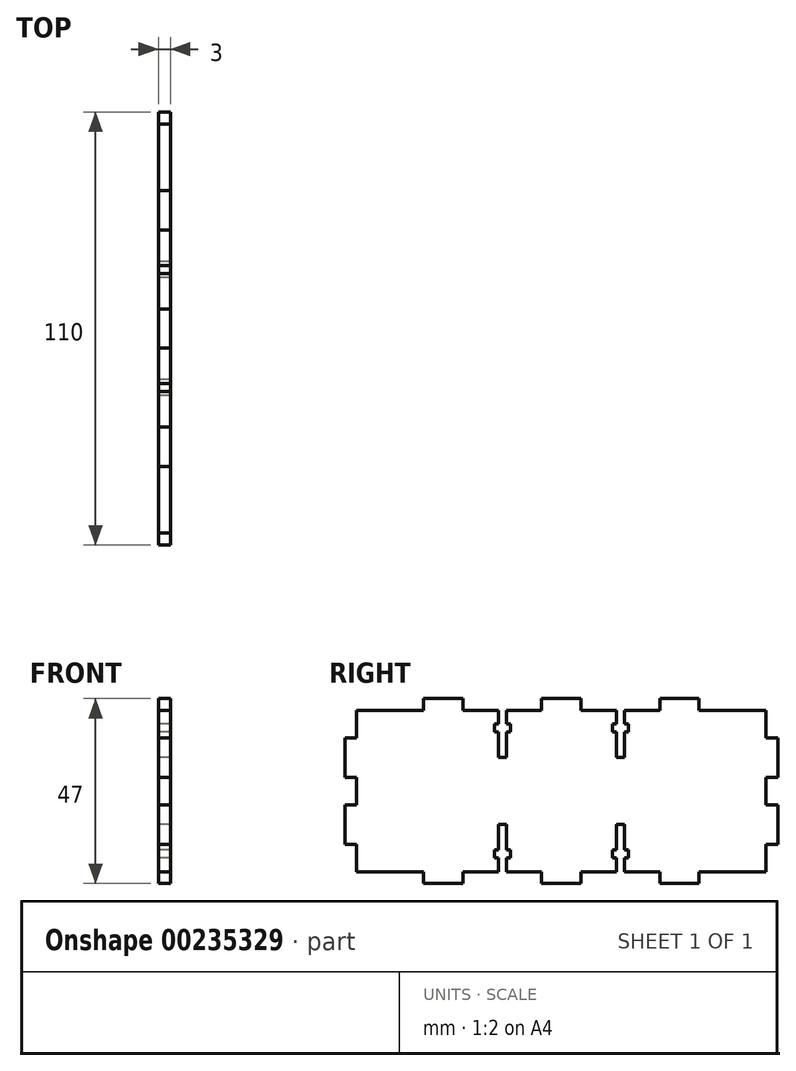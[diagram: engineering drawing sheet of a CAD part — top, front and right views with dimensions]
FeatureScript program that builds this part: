
annotation { "Feature Type Name" : "Feature", "Feature Type Description" : "" }
export const myFeature = defineFeature(function(context is Context, id is Id, definition is map)
    precondition{}
    {
        {
            var Q0;
            Q0=qCreatedBy(makeId("Right.planeOp"),FACE);
            var sketch = newSketch(context, id + "F0", { "sketchPlane" : qUnion([Q0])});
            skLineSegment(sketch, "E0", {"start": v(0, 0) * mm, "end": v(0, 7) * mm});
            skLineSegment(sketch, "E1", {"start": v(0, 7) * mm, "end": v(-3, 7) * mm});
            skLineSegment(sketch, "E2", {"start": v(-3, 7) * mm, "end": v(-3, 17) * mm});
            skLineSegment(sketch, "E3", {"start": v(-3, 17) * mm, "end": v(0, 17) * mm});
            skLineSegment(sketch, "E4", {"start": v(0, 17) * mm, "end": v(0, 24) * mm});
            skLineSegment(sketch, "E5", {"start": v(0, 24) * mm, "end": v(-3, 24) * mm});
            skLineSegment(sketch, "E6", {"start": v(-3, 24) * mm, "end": v(-3, 34) * mm});
            skLineSegment(sketch, "E7", {"start": v(-3, 34) * mm, "end": v(0, 34) * mm});
            skLineSegment(sketch, "E8", {"start": v(0, 34) * mm, "end": v(0, 41) * mm});
            skLineSegment(sketch, "E9", {"start": v(0, 41) * mm, "end": v(17, 41) * mm});
            skLineSegment(sketch, "E10", {"start": v(17, 41) * mm, "end": v(17, 44) * mm});
            skLineSegment(sketch, "E11", {"start": v(17, 44) * mm, "end": v(27, 44) * mm});
            skLineSegment(sketch, "E12", {"start": v(27, 44) * mm, "end": v(27, 41) * mm});
            skLineSegment(sketch, "E13", {"start": v(27, 41) * mm, "end": v(36, 41) * mm});
            skLineSegment(sketch, "E14", {"start": v(47, 41) * mm, "end": v(47, 44) * mm});
            skLineSegment(sketch, "E15", {"start": v(47, 44) * mm, "end": v(52, 44) * mm});
            skLineSegment(sketch, "E16.MirrorCS", {"start": v(47, 0) * mm, "end": v(47, -3) * mm});
            skLineSegment(sketch, "E17.MirrorCS", {"start": v(27, -3) * mm, "end": v(27, 0) * mm});
            skLineSegment(sketch, "E18.MirrorCS", {"start": v(17, 0) * mm, "end": v(17, -3) * mm});
            skLineSegment(sketch, "E19.MirrorCS", {"start": v(47, -3) * mm, "end": v(52, -3) * mm});
            skLineSegment(sketch, "E20.MirrorCS", {"start": v(27, 0) * mm, "end": v(33.54, 0) * mm});
            skLineSegment(sketch, "E21.MirrorCS", {"start": v(0, 0) * mm, "end": v(17, 0) * mm});
            skLineSegment(sketch, "E22.MirrorCS", {"start": v(17, -3) * mm, "end": v(27, -3) * mm});
            skLineSegment(sketch, "E23.MirrorCS", {"start": v(57, -3) * mm, "end": v(52, -3) * mm});
            skLineSegment(sketch, "E24.MirrorCS", {"start": v(57, 44) * mm, "end": v(52, 44) * mm});
            skLineSegment(sketch, "E25.top", {"start": v(36, 29) * mm, "end": v(38, 29) * mm});
            skLineSegment(sketch, "E25.left", {"start": v(36, 41) * mm, "end": v(36, 37.5) * mm});
            skLineSegment(sketch, "E25.right", {"start": v(38, 41) * mm, "end": v(38, 37.5) * mm});
            skLineSegment(sketch, "E26.MirrorCS", {"start": v(33.54, 41) * mm, "end": v(36, 41) * mm});
            skPoint(sketch, "E27.endSnap0", {"position": v(37, 29) * mm});
            skLineSegment(sketch, "E28.bottom", {"start": v(35, 37.5) * mm, "end": v(36, 37.5) * mm});
            skLineSegment(sketch, "E28.top", {"start": v(35, 35.5) * mm, "end": v(36, 35.5) * mm});
            skLineSegment(sketch, "E28.left", {"start": v(35, 37.5) * mm, "end": v(35, 35.5) * mm});
            skLineSegment(sketch, "E28.right", {"start": v(39, 37.5) * mm, "end": v(39, 35.5) * mm});
            skLineSegment(sketch, "E29.trimOffspring", {"start": v(38, 41) * mm, "end": v(47, 41) * mm});
            skLineSegment(sketch, "E30.trimOffspring", {"start": v(38, 41) * mm, "end": v(38.1, 41) * mm});
            skLineSegment(sketch, "E31.trimOffspring", {"start": v(38, 37.5) * mm, "end": v(39, 37.5) * mm});
            skLineSegment(sketch, "E32.trimOffspring", {"start": v(36, 35.5) * mm, "end": v(36, 29) * mm});
            skLineSegment(sketch, "E33.trimOffspring", {"start": v(38, 35.5) * mm, "end": v(38, 29) * mm});
            skLineSegment(sketch, "E34.trimOffspring", {"start": v(38, 35.5) * mm, "end": v(39, 35.5) * mm});
            skLineSegment(sketch, "E35.MirrorCS", {"start": v(38, 0) * mm, "end": v(38.1, 0) * mm});
            skLineSegment(sketch, "E36.MirrorCS", {"start": v(35, 3.5) * mm, "end": v(36, 3.5) * mm});
            skLineSegment(sketch, "E37.MirrorCS", {"start": v(38, 5.5) * mm, "end": v(39, 5.5) * mm});
            skLineSegment(sketch, "E38.MirrorCS", {"start": v(35, 5.5) * mm, "end": v(36, 5.5) * mm});
            skLineSegment(sketch, "E39.MirrorCS", {"start": v(38, 3.5) * mm, "end": v(39, 3.5) * mm});
            skLineSegment(sketch, "E40.MirrorCS", {"start": v(36, 12) * mm, "end": v(38, 12) * mm});
            skLineSegment(sketch, "E41.MirrorCS", {"start": v(36, 5.5) * mm, "end": v(36, 12) * mm});
            skLineSegment(sketch, "E42.MirrorCS", {"start": v(38, 5.5) * mm, "end": v(38, 12) * mm});
            skLineSegment(sketch, "E43.MirrorCS", {"start": v(35, 3.5) * mm, "end": v(35, 5.5) * mm});
            skLineSegment(sketch, "E44.MirrorCS", {"start": v(36, 0) * mm, "end": v(36, 3.5) * mm});
            skLineSegment(sketch, "E45.MirrorCS", {"start": v(39, 3.5) * mm, "end": v(39, 5.5) * mm});
            skLineSegment(sketch, "E46.MirrorCS", {"start": v(38, 0) * mm, "end": v(38, 3.5) * mm});
            skPoint(sketch, "E47.MirrorP", {"position": v(37, 12) * mm});
            skLineSegment(sketch, "E48.MirrorCS", {"start": v(33.54, 0) * mm, "end": v(36, 0) * mm});
            skLineSegment(sketch, "E49.trimOffspring", {"start": v(38, 0) * mm, "end": v(47, 0) * mm});
            skLineSegment(sketch, "E50", {"start": v(52, 44) * mm, "end": v(52, -3) * mm, "construction": true});
            skLineSegment(sketch, "E51.MirrorCS", {"start": v(66, 41) * mm, "end": v(65.9, 41) * mm});
            skLineSegment(sketch, "E52.MirrorCS", {"start": v(66, 0) * mm, "end": v(65.9, 0) * mm});
            skLineSegment(sketch, "E53.MirrorCS", {"start": v(69, 3.5) * mm, "end": v(68, 3.5) * mm});
            skLineSegment(sketch, "E54.MirrorCS", {"start": v(66, 5.5) * mm, "end": v(65, 5.5) * mm});
            skLineSegment(sketch, "E55.MirrorCS", {"start": v(66, 3.5) * mm, "end": v(65, 3.5) * mm});
            skLineSegment(sketch, "E56.MirrorCS", {"start": v(69, 5.5) * mm, "end": v(68, 5.5) * mm});
            skLineSegment(sketch, "E57.MirrorCS", {"start": v(69, 35.5) * mm, "end": v(68, 35.5) * mm});
            skLineSegment(sketch, "E58.MirrorCS", {"start": v(66, 37.5) * mm, "end": v(65, 37.5) * mm});
            skLineSegment(sketch, "E59.MirrorCS", {"start": v(66, 35.5) * mm, "end": v(65, 35.5) * mm});
            skLineSegment(sketch, "E60.MirrorCS", {"start": v(69, 37.5) * mm, "end": v(68, 37.5) * mm});
            skLineSegment(sketch, "E61.MirrorCS", {"start": v(68, 29) * mm, "end": v(66, 29) * mm});
            skLineSegment(sketch, "E62.MirrorCS", {"start": v(107, 17) * mm, "end": v(104, 17) * mm});
            skLineSegment(sketch, "E63.MirrorCS", {"start": v(68, 12) * mm, "end": v(66, 12) * mm});
            skLineSegment(sketch, "E64.MirrorCS", {"start": v(70.46, 41) * mm, "end": v(68, 41) * mm});
            skLineSegment(sketch, "E65.MirrorCS", {"start": v(65, 3.5) * mm, "end": v(65, 5.5) * mm});
            skLineSegment(sketch, "E66.MirrorCS", {"start": v(66, 41) * mm, "end": v(57, 41) * mm});
            skLineSegment(sketch, "E67.MirrorCS", {"start": v(77, 0) * mm, "end": v(70.46, 0) * mm});
            skLineSegment(sketch, "E68.MirrorCS", {"start": v(107, 7) * mm, "end": v(107, 17) * mm});
            skLineSegment(sketch, "E69.MirrorCS", {"start": v(104, 17) * mm, "end": v(104, 24) * mm});
            skLineSegment(sketch, "E70.MirrorCS", {"start": v(104, 24) * mm, "end": v(107, 24) * mm});
            skLineSegment(sketch, "E71.MirrorCS", {"start": v(66, 0) * mm, "end": v(66, 3.5) * mm});
            skLineSegment(sketch, "E72.MirrorCS", {"start": v(66, 41) * mm, "end": v(66, 37.5) * mm});
            skLineSegment(sketch, "E73.MirrorCS", {"start": v(107, 24) * mm, "end": v(107, 34) * mm});
            skLineSegment(sketch, "E74.MirrorCS", {"start": v(104, 34) * mm, "end": v(104, 41) * mm});
            skLineSegment(sketch, "E75.MirrorCS", {"start": v(107, 34) * mm, "end": v(104, 34) * mm});
            skLineSegment(sketch, "E76.MirrorCS", {"start": v(87, 41) * mm, "end": v(87, 44) * mm});
            skLineSegment(sketch, "E77.MirrorCS", {"start": v(104, 41) * mm, "end": v(87, 41) * mm});
            skLineSegment(sketch, "E78.MirrorCS", {"start": v(87, 44) * mm, "end": v(77, 44) * mm});
            skLineSegment(sketch, "E79.MirrorCS", {"start": v(77, 44) * mm, "end": v(77, 41) * mm});
            skLineSegment(sketch, "E80.MirrorCS", {"start": v(66, 35.5) * mm, "end": v(66, 29) * mm});
            skLineSegment(sketch, "E81.MirrorCS", {"start": v(68, 41) * mm, "end": v(68, 37.5) * mm});
            skPoint(sketch, "E82.MirrorP", {"position": v(67, 29) * mm});
            skLineSegment(sketch, "E83.MirrorCS", {"start": v(57, 0) * mm, "end": v(57, -3) * mm});
            skLineSegment(sketch, "E84.MirrorCS", {"start": v(66, 5.5) * mm, "end": v(66, 12) * mm});
            skLineSegment(sketch, "E85.MirrorCS", {"start": v(104, 0) * mm, "end": v(87, 0) * mm});
            skPoint(sketch, "E86.MirrorP", {"position": v(67, 12) * mm});
            skLineSegment(sketch, "E87.MirrorCS", {"start": v(70.46, 0) * mm, "end": v(68, 0) * mm});
            skLineSegment(sketch, "E88.MirrorCS", {"start": v(77, -3) * mm, "end": v(77, 0) * mm});
            skLineSegment(sketch, "E89.MirrorCS", {"start": v(69, 3.5) * mm, "end": v(69, 5.5) * mm});
            skLineSegment(sketch, "E90.MirrorCS", {"start": v(69, 37.5) * mm, "end": v(69, 35.5) * mm});
            skLineSegment(sketch, "E91.MirrorCS", {"start": v(87, 0) * mm, "end": v(87, -3) * mm});
            skLineSegment(sketch, "E92.MirrorCS", {"start": v(65, 37.5) * mm, "end": v(65, 35.5) * mm});
            skLineSegment(sketch, "E93.MirrorCS", {"start": v(68, 0) * mm, "end": v(68, 3.5) * mm});
            skLineSegment(sketch, "E94.MirrorCS", {"start": v(87, -3) * mm, "end": v(77, -3) * mm});
            skLineSegment(sketch, "E95.MirrorCS", {"start": v(68, 5.5) * mm, "end": v(68, 12) * mm});
            skLineSegment(sketch, "E96.MirrorCS", {"start": v(66, 0) * mm, "end": v(57, 0) * mm});
            skLineSegment(sketch, "E97.MirrorCS", {"start": v(68, 35.5) * mm, "end": v(68, 29) * mm});
            skLineSegment(sketch, "E98.MirrorCS", {"start": v(77, 41) * mm, "end": v(68, 41) * mm});
            skLineSegment(sketch, "E99.MirrorCS", {"start": v(57, 41) * mm, "end": v(57, 44) * mm});
            skLineSegment(sketch, "E100.MirrorCS", {"start": v(104, 0) * mm, "end": v(104, 7) * mm});
            skLineSegment(sketch, "E101.MirrorCS", {"start": v(104, 7) * mm, "end": v(107, 7) * mm});
            skSolve(sketch);
        }
        {
            var Q0;
            Q0=qSketchRegion(id+"F0",true);
            extrude(context, id + "F1", {"entities" : qUnion([Q0]), "depth" : 3 * mm});
        }
    });
